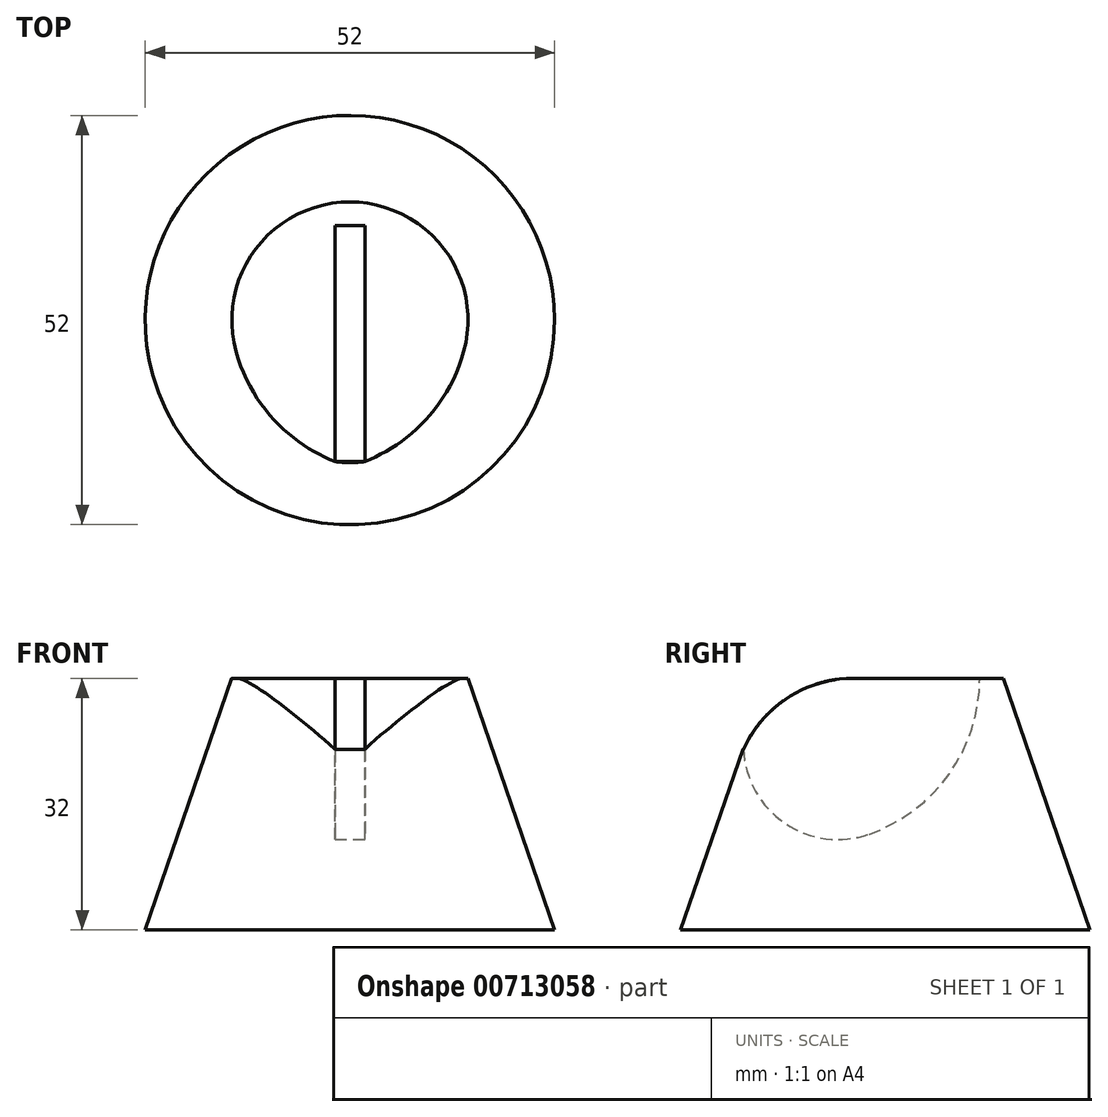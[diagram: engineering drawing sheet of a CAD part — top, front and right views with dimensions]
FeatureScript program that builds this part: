
annotation { "Feature Type Name" : "Feature", "Feature Type Description" : "" }
export const myFeature = defineFeature(function(context is Context, id is Id, definition is map)
    precondition{}
    {
        {
            var Q0;
            Q0=qCreatedBy(makeId("Top.planeOp"),FACE);
            var sketch = newSketch(context, id + "F0", { "sketchPlane" : qUnion([Q0])});
            skCircle(sketch, "E0", {"center": v(0, 0) * mm, "radius": 26 * mm});
            skSolve(sketch);
        }
        {
            var Q0;
            Q0=qCreatedBy(makeId("Top.planeOp"),FACE);
            cPlane(context, id + "F1", {"entities" : qUnion([Q0]), "cplaneType" : CPlaneType.OFFSET, "offset" : 32 * mm, "width" : 150 * mm, "height" : 150 * mm});
        }
        {
            var Q0;
            Q0=qCreatedBy(id+"F1.planeOp",FACE);
            var sketch = newSketch(context, id + "F2", { "sketchPlane" : qUnion([Q0])});
            skCircle(sketch, "E1", {"center": v(0, 0) * mm, "radius": 15 * mm});
            skSolve(sketch);
        }
        {
            var Q0;
            Q0=makeQuery(id+"F0.imprint","IMPRINT",FACE,{"disambiguationData":[TD([[makeQuery(id+"F0.imprint","IMPRINT",EDGE,{"derivedFrom":sQuery(id+"F0.wireOp",EDGE,"E0")}),1.0]])]});
            var Q1;
            Q1=makeQuery(id+"F2.imprint","IMPRINT",FACE,{"disambiguationData":[TD([[makeQuery(id+"F2.imprint","IMPRINT",EDGE,{"derivedFrom":sQuery(id+"F2.wireOp",EDGE,"E1")}),1.0]])]});
            loft(context, id + "F3", {"sheetProfilesArray" : [{ "sheetProfileEntities" : qUnion([Q0]) }, { "sheetProfileEntities" : qUnion([Q1]) }]});
        }
        {
            var Q0;
            Q0=makeQuery(id+"F3.opLoft","CAP_FACE",FACE,{"disambiguationData":[OSD([makeQuery(id+"F2.imprint","IMPRINT",FACE,{"disambiguationData":[TD([[makeQuery(id+"F2.imprint","IMPRINT",EDGE,{"derivedFrom":sQuery(id+"F2.wireOp",EDGE,"E1")}),1.0]])]})])],"isStart":true});
            var sketch = newSketch(context, id + "F4", { "sketchPlane" : qUnion([Q0])});
            skLineSegment(sketch, "E2", {"start": v(0, 15) * mm, "end": v(0, 12) * mm, "construction": true});
            skLineSegment(sketch, "E3", {"start": v(0, 0) * mm, "end": v(-1.9, 0) * mm, "construction": true});
            skLineSegment(sketch, "E4", {"start": v(-1.9, 0) * mm, "end": v(1.9, 0) * mm, "construction": true});
            skLineSegment(sketch, "E5", {"start": v(1.9, 0) * mm, "end": v(1.9, 12) * mm});
            skLineSegment(sketch, "E6", {"start": v(1.9, 12) * mm, "end": v(-1.9, 12) * mm});
            skLineSegment(sketch, "E7", {"start": v(-1.9, 12) * mm, "end": v(-1.9, 0) * mm});
            skLineSegment(sketch, "E8", {"start": v(-1.9, 12) * mm, "end": v(-1.9, -18) * mm});
            skLineSegment(sketch, "E9", {"start": v(-1.9, -18) * mm, "end": v(1.9, -18) * mm});
            skLineSegment(sketch, "E10", {"start": v(1.9, -18) * mm, "end": v(1.9, 0) * mm});
            skSolve(sketch);
        }
        {
            var Q0;
            Q0 = qSketchRegion(id + "F4", true);
            extrude(context, id + "F5", {"entities" : qUnion([Q0]), "operationType" : NewBodyOperationType.REMOVE, "oppositeDirection" : true, "depth" : 21 * mm, "offsetDistance" : 25 * mm});
        }
        {
            var Q0;
            Q0=qCreatedBy(makeId("Front.planeOp"),FACE);
            var sketch = newSketch(context, id + "F6", { "sketchPlane" : qUnion([Q0])});
            skPoint(sketch, "E11.0", {"position": v(-1.9, 22.98) * mm});
            skPoint(sketch, "E12.0", {"position": v(1.9, 22.98) * mm});
            skLineSegment(sketch, "E13", {"start": v(-1.9, 22.98) * mm, "end": v(1.9, 22.98) * mm});
            skLineSegment(sketch, "E14", {"start": v(-1.9, 22.98) * mm, "end": v(-1.9, 24.45) * mm});
            skLineSegment(sketch, "E15", {"start": v(-1.9, 24.45) * mm, "end": v(1.9, 24.45) * mm});
            skLineSegment(sketch, "E16", {"start": v(1.9, 24.45) * mm, "end": v(1.9, 22.98) * mm});
            skSolve(sketch);
        }
        {
            var Q0;
            Q0 = qSketchRegion(id + "F6", true);
            extrude(context, id + "F7", {"entities" : qUnion([Q0]), "operationType" : NewBodyOperationType.REMOVE, "depth" : 50 * mm, "offsetDistance" : 25 * mm});
        }
        {
            var Q0;
            Q0=qCreatedBy(makeId("Right.planeOp"),FACE);
            var sketch = newSketch(context, id + "F8", { "sketchPlane" : qUnion([Q0])});
            skPoint(sketch, "E17.0", {"position": v(15, 32) * mm});
            skLineSegment(sketch, "E18", {"start": v(15, 32) * mm, "end": v(-4, 32) * mm, "construction": true});
            skPoint(sketch, "E19.0", {"position": v(-18, 22.98) * mm});
            skArc(sketch, "E20", {"start": v(-4, 32) * mm, "mid": v(-12.33, 29.55) * mm, "end": v(-18, 22.98) * mm});
            skLineSegment(sketch, "E21", {"start": v(-4, 32) * mm, "end": v(-18, 32) * mm});
            skLineSegment(sketch, "E22", {"start": v(-18, 32) * mm, "end": v(-18, 22.98) * mm});
            skSolve(sketch);
        }
        {
            var Q0;
            Q0 = qSketchRegion(id + "F8", true);
            extrude(context, id + "F9", {"entities" : qUnion([Q0]), "operationType" : NewBodyOperationType.REMOVE, "endBound" : BoundingType.SYMMETRIC, "oppositeDirection" : true, "depth" : 50 * mm, "offsetDistance" : 25 * mm});
        }
        {
            var Q0;
            Q0=makeQuery(id+"F5.boolean.opBoolean","COPY",EDGE,{"derivedFrom":makeQuery(id+"F5.opExtrude","CAP_EDGE",EDGE,{"disambiguationData":[OSD([sQuery(id+"F4.wireOp",EDGE,"E6")])],"isStart":false})});
            fillet(context, id + "F10", {"entities" : qUnion([Q0]), "radius" : 21 * mm, "tangentPropagation" : true, "allowEdgeOverflow" : false});
        }
        {
            var Q0;
            Q0=makeQuery(id+"F5.boolean.opBoolean","COPY",EDGE,{"derivedFrom":makeQuery(id+"F5.opExtrude","CAP_EDGE",EDGE,{"disambiguationData":[OSD([sQuery(id+"F4.wireOp",EDGE,"E9")])],"isStart":false})});
            fillet(context, id + "F11", {"entities" : qUnion([Q0]), "radius" : 12 * mm, "tangentPropagation" : true, "allowEdgeOverflow" : false});
        }
    });
